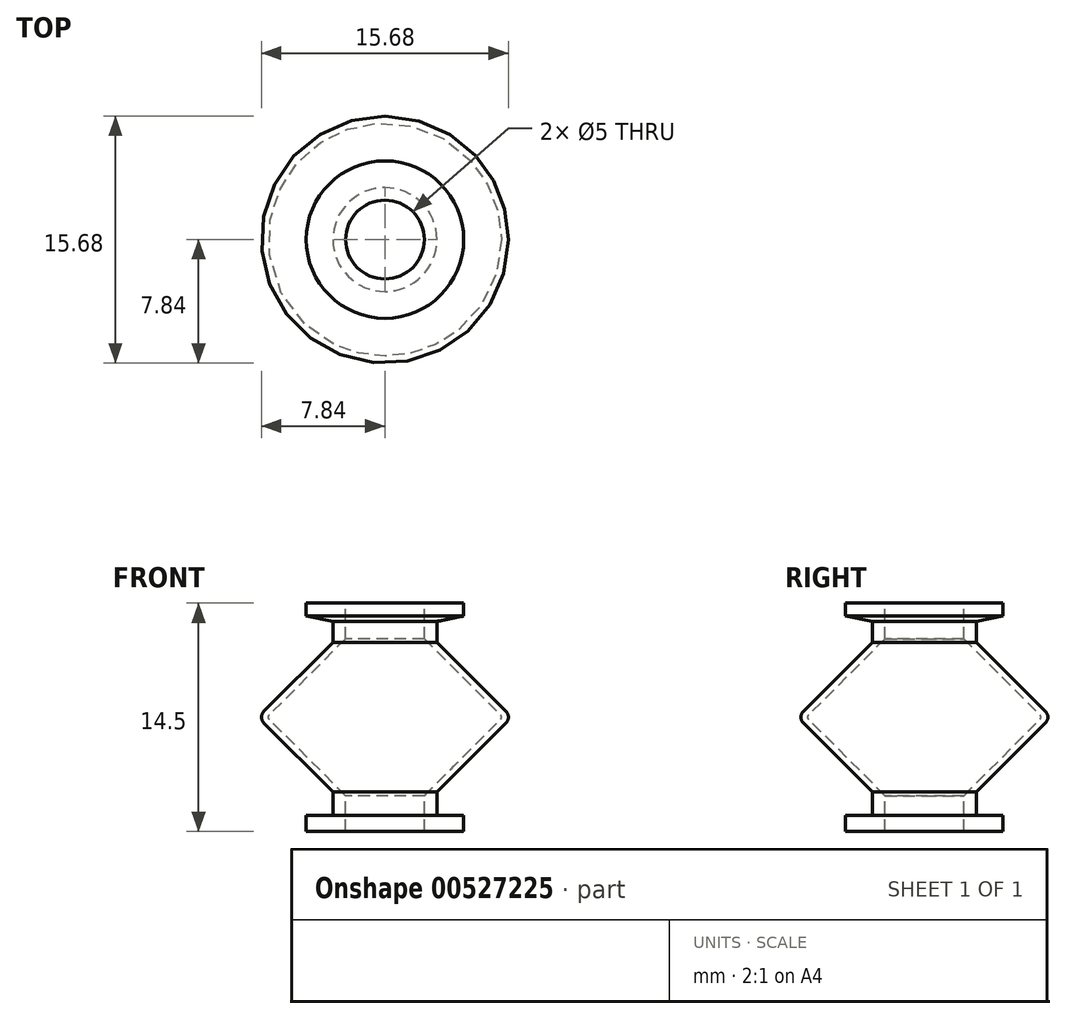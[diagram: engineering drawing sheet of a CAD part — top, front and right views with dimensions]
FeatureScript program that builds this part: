
annotation { "Feature Type Name" : "Feature", "Feature Type Description" : "" }
export const myFeature = defineFeature(function(context is Context, id is Id, definition is map)
    precondition{}
    {
        {
            var Q0;
            Q0=qCreatedBy(makeId("Front.planeOp"),FACE);
            var sketch = newSketch(context, id + "F0", { "sketchPlane" : qUnion([Q0])});
            skLineSegment(sketch, "E0", {"start": v(-2.5, 7.25) * mm, "end": v(-5, 7.25) * mm});
            skLineSegment(sketch, "E1", {"start": v(-5, 7.25) * mm, "end": v(-5, 6.43) * mm});
            skLineSegment(sketch, "E2", {"start": v(-3.3, 6.09) * mm, "end": v(-3.3, 4.75) * mm});
            skLineSegment(sketch, "E3", {"start": v(-2.5, 7.25) * mm, "end": v(-2.5, 4.98) * mm});
            skLineSegment(sketch, "E4.MirrorCS", {"start": v(-3.3, -4.75) * mm, "end": v(-7.7, -0.35) * mm});
            skLineSegment(sketch, "E5.MirrorCS", {"start": v(-3.3, -6.25) * mm, "end": v(-3.3, -4.75) * mm});
            skLineSegment(sketch, "E6.MirrorCS", {"start": v(-5, -6.25) * mm, "end": v(-3.3, -6.25) * mm});
            skLineSegment(sketch, "E7.MirrorCS", {"start": v(-5, -7.25) * mm, "end": v(-5, -6.25) * mm});
            skLineSegment(sketch, "E8.MirrorCS", {"start": v(-2.5, -7.25) * mm, "end": v(-5, -7.25) * mm});
            skLineSegment(sketch, "E9.MirrorCS", {"start": v(-2.5, -7.25) * mm, "end": v(-2.5, -4.98) * mm});
            skLineSegment(sketch, "E10", {"start": v(0, 8.81) * mm, "end": v(0, -10.41) * mm, "construction": true});
            skLineSegment(sketch, "E11.MirrorCS", {"start": v(-3.3, 4.75) * mm, "end": v(-7.7, 0.35) * mm});
            skLineSegment(sketch, "E12", {"start": v(-7.34, 0.14) * mm, "end": v(-2.5, 4.98) * mm});
            skArc(sketch, "E13", {"start": v(-7.7, 0.35) * mm, "mid": v(-7.84, 0) * mm, "end": v(-7.7, -0.35) * mm});
            skArc(sketch, "E14", {"start": v(-7.34, 0.14) * mm, "mid": v(-7.4, 0) * mm, "end": v(-7.34, -0.14) * mm});
            skLineSegment(sketch, "E15.MirrorCS", {"start": v(-7.34, -0.14) * mm, "end": v(-2.5, -4.98) * mm});
            skLineSegment(sketch, "E16", {"start": v(-5, 6.43) * mm, "end": v(-3.3, 6.09) * mm});
            skSolve(sketch);
        }
        {
            var Q0;
            Q0 = qSketchRegion(id + "F0", true);
            var Q1;
            Q1=sQuery(id+"F0.wireOp",EDGE,"E10");
            revolve(context, id + "F1", {"entities" : qUnion([Q0]), "axis" : qUnion([Q1]), "revolveType" : RevolveType.FULL});
        }
    });
